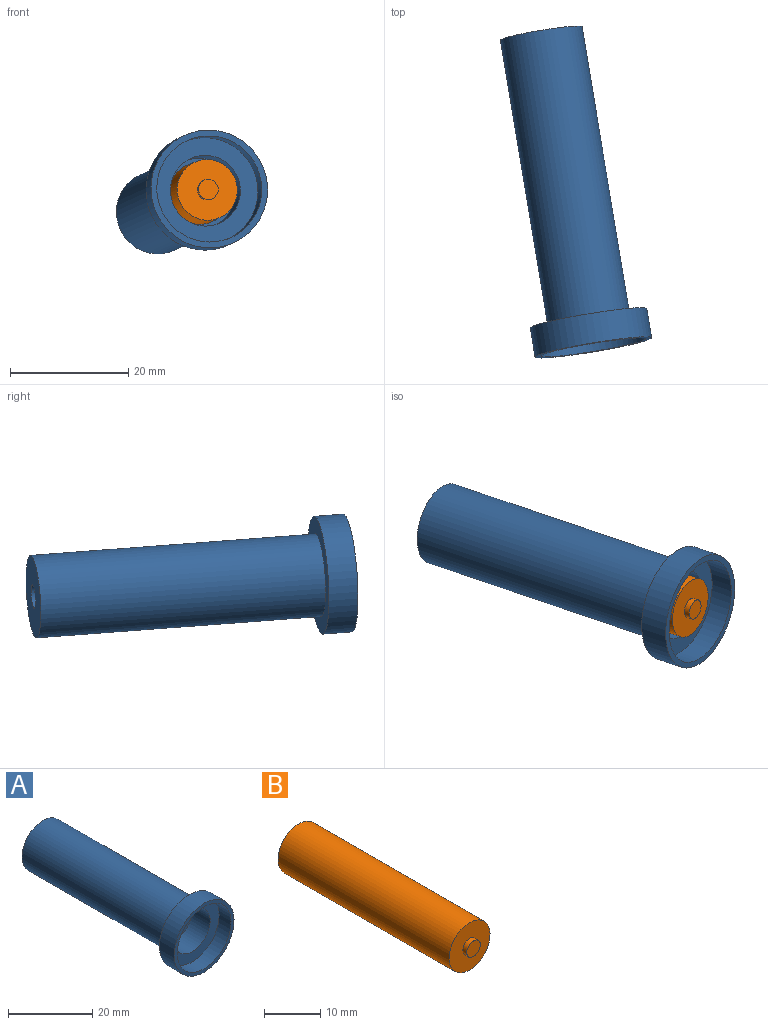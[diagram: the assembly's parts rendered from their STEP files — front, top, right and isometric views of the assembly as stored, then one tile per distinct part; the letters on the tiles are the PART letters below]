
ASSEMBLY  parts=2 mates=1
PART A: 12 faces, bbox 20x54x20 mm
  f0: cylinder r=5.25mm len=41mm, axis (0,-1,0), area 1352.5mm2, adj f2,f10
  f1: cylinder r=7mm len=49mm, axis (0,1,0), area 2155.1mm2, adj f3,f5
  f2: plane 10.5x10.5mm, normal (0,-1,0), area 74mm2, adj f0,f4
  f3: plane 14x14mm, normal (0,1,0), area 141.4mm2, adj f1,f4
  f4: cylinder r=2mm len=4mm, axis (0,1,0), area 37.7mm2, adj f2,f3
  f5: plane 20x20mm, normal (0,1,0), area 160.2mm2, adj f1,f7
  f6: plane 20x20mm, normal (0,-1,0), area 59.7mm2, adj f7,f8
  f7: cylinder r=10mm len=20mm, axis (0,1,0), area 314.2mm2, adj f5,f6
  f8: cylinder r=9mm len=18mm, axis (0,-1,0), area 226.2mm2, adj f6,f9
  f9: plane 18x18mm, normal (0,-1,0), area 141.4mm2, adj f8,f11
  f10: plane 12x12mm, normal (0,-1,0), area 26.5mm2, adj f0,f11
  f11: cylinder r=6mm len=12mm, axis (0,-1,0), area 226.2mm2, adj f9,f10
PART B: 5 faces, bbox 10.3x44x10.3 mm
  f0: cylinder r=5.15mm len=43mm, axis (0,1,0), area 1391.4mm2, adj f1,f2
  f1: plane 10.3x10.3mm, normal (0,-1,0), area 74.2mm2, adj f0,f3
  f2: plane 10.3x10.3mm, normal (0,1,0), area 83.3mm2, adj f0
  f3: cylinder r=1.7mm len=3.4mm, axis (0,1,0), area 10.7mm2, adj f1,f4
  f4: plane 3.4x3.4mm, normal (0,-1,0), area 9.1mm2, adj f3
PLACE A rot(axis=(-0.11,-0.89,0.43),23.2deg) t=(0.04,-116.52,2.12)mm
PLACE B rot(axis=(-0.13,0.99,0.08),69.9deg) t=(1.01,-122.37,2.56)mm
MATE cylindrical B.f0 <-> A.f1  axis (-0.16,0.98,-0.07) through (1.01,-122.37,2.56)mm
